# Revit family: Lighting_Pendants_Pholc_Donna_Circle-600
name_source: partatom
category: Lighting Fixtures
revit_build: Autodesk Revit 2017 (Build: 20190508_0315(x64)
units: mm (PartAtom-declared; Revit-internal decimal feet)

## family parameters
Always vertical = Yes
Cut with Voids When Loaded = No
Host = Ceiling
Light Source = No
Part Type = Normal
Room Calculation Point = No
Round Connector Dimension = Use Diameter
Shared = No

## types (2) — shared parameters
Apparent Load = 0 VA
BIMObjectName = Lighting_Pendants_Pholc_Donna_Circle-600
Brand = Pholc
Category = Pendant
Collection = Donna
ConvergoRefNr = 0103-1912-0003-SE
Description = The Donna pendant lamp projects the feeling of a soft pleated textile, although it’s actually made from thin, light aluminium. Its form is inspired by the chic fabrics used in high fashion and the challenges of creating this softness using a hard material instead of a textile. A beautiful and versatile piece with an expressive personality; equally at home in all environments. For larger spaces the Donna Line and Donna Circle can be selected in four, six or eight lamp variants, casting a warm direct light downwards.
Designer = Nina Jobs & Stina Sandwall
DurationUnit = Hours
ElectricalDeviceNominalPower = 7 W
Features = Textile cable. Cable length 500 cm. Socket GU10.
HasProtectiveEarth = No
IP_Code = IP 20
IfcExportAs = IfcLightFixtureType
IfcExportType = NOTDEFINED
InsulationStandardClass = Class II
LightFixtureMountingType = Suspended
LightFixturePlacingType = Ceilling
Manufacturer = Pholc
ManufacturerName = Pholc
ManufacturerURL = www.pholc.se/
Material = Aluminium & textile
NBSDescription = General purpose luminaires
NBSReference = 90-60-50/405
Name = Pholc_Donna_Circle-600
NominalCurrent = 0 A
NominalDepth = 612 mm
NominalFrequencyRange = 0 Hz
NominalLength = 663 mm
NominalVoltage = 230 V
NominalVoltageCalc = 230 V
NumberOfPoles = 1
NumberOfSources = 1
PhaseAngle = 0.00°
ProductInformation = The Donna pendant lamp projects the feeling of a soft pleated textile, although it’s actually made from thin, light aluminium.
Shape = Sculptured
Size = 600x600x140 mm
TotalWattage = 7 W
URL = https://www.pholc.se
Uniclass2 = Pr_70_70_49_86
Uniclass2015Description = Suspended luminaires
Uniclass2015Reference = Pr_70_70_48_86
UsageCurrent = 0 A
Version = 1
VersionDate = 21/04/2020
WarrantyDurationUnit = Years
zero-valued in all types: DefaultElevation, MaintenanceFactor

## per-type parameters (varying)
| type | ArticleNumber | AssetType | Color | LightFixtureMainMaterial | ModelReference |
| Donna Pendant Circle 600 - Black Ink | 963165 | Fixed | Black Ink | Black ink | 963165 |
| Donna Pendant Circle 600 - Linen | 963163 |  | Linen | Linen | 963163 |

note: column(s) folded — value = type name in every type: Model

## geometry (parser evidence)
native form markers: Sweep x4
no freeform markers — native parametric forms only
